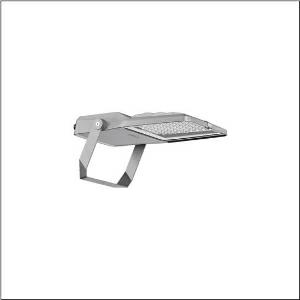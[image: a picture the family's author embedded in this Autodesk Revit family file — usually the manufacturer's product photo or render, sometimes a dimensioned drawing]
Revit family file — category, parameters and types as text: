
# Revit family: floodlight_fl_21_mini___pl43_5xa7775b2a1a_e8ea
name_source: partatom
category: Lighting Fixtures
units: mm (PartAtom-declared; Revit-internal decimal feet)

## family parameters
Cut with Voids When Loaded = No
Host = Face
Light Source = No
Part Type = Normal
Room Calculation Point = No
Round Connector Dimension = Use Diameter
Shared = No

## types (1)
- --- (1 x LED, 6390 lm, 45.7 W, 3000K)
    Apparent Load = 46 VA
    CIE Flux Codes = 27 78 99 100 100
    Color Rendering = 70
    Color Temperature = 3000K
    Default Elevation = 1800 mm
    Description = Floodlight FL 21 mini, floodlight, primary light control with lens, of PMMA, primary optical cover: protective disc, of toughened safety glass, transparent, light distribution: PL43, light emission: direct distribution, installation type: surface-mounted, LED, High Power LED, rated luminous flux: 6.390lm, luminous efficacy: 140lm/W, light colour: 730, colour temperature: 3000K, control gear: Smart Interface (Zhaga), control: flexible luminous flux parameterisation, time-dependent luminous flux control, constant luminous flux control, overheat protection, pre-setting: logarithmic dimming characteristic, with terminal, 6-pole, mains connection: 220..240V, AC, 50/60Hz, start of lifetime: 46W, end of service life: 48W, reduction: 22W, luminaire housing, of diecast aluminium, powder-coated, SITECO metallic grey (DB 702S), corrosivity category C5 mid according to DIN EN ISO 12944, suitable for swimming pools, chlorine-resistant, sealing non-destructively replaceable, mounting bracket, of steel, galvanised, powder-coated, SITECO metallic grey (DB 702S), Smart Interface above, protection rating (complete): IP66, insulation class (complete): insulation class II (safety insulation), certification: CE, ENEC, VDE, protection symbol: D, impact resistance: IK08, permissible operating ambient temperature: -40..+40°C, permissible operating ambient temperature for outdoor applications: -40..+50°C, standard: DIN EN 12944, LABS conformity tested according to VDMA 24364:2018-05, packaging unit: 1 piece

Light Distribution: PL43
    Height = 70 mm
    Lamp = 1 x LED
    Lamp Light Flux = 6390 lm
    Lamp Power = 45.7 W
    Lamp count = 1
    Length = 485 mm
    Luminous efficacy = 140 lm/W
    Manufacturer = Siteco
    ModVariant = No
    Model = 5XA7775B2A1A
    Number of Poles = 1
    OnlyDefault = Yes
    Power Factor = 1
    Product Name = Floodlight FL 21 mini | PL43
    Product group = floodlight | pylon annexe
    ProductGroupID = 6201
    Protection Class = Protection class II
    Protection Degree = IP 66
    RLX_Detail_Level = 1
    RLX_Emergency_Light_Flux = 0 lm
    RLX_Emergency_Type = 0
    RLX_Emergency_Type_DB = No
    RlxData = <blob elided: 95909 chars, md5=bfd22428>
    Socket = socket
    Standby Power = 0 W
    System Light Flux = 6390 lm
    System Power = 46 W
    Type Comments = factory setting: luminous flux: 100 % | dim-lin: 254 | 463 mA
    Type Image = l_1006845.jpg
    URL = http://relux.com
    VarID = @adj_160787
    Voltage = 0 V
    Weight = 0.00 kg
    Width = 337 mm

## geometry (parser evidence)
native form markers: Blend x4, Sweep x11
no freeform markers — native parametric forms only
